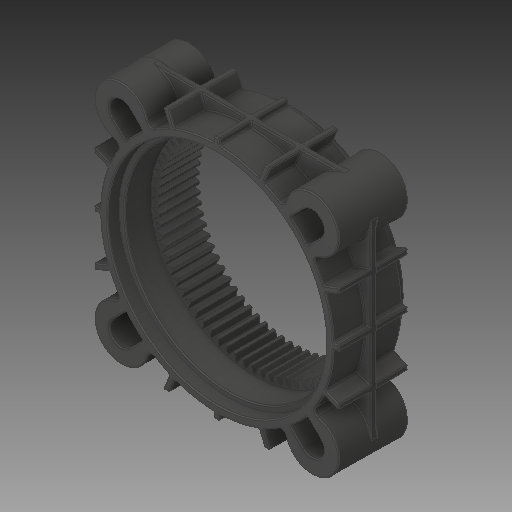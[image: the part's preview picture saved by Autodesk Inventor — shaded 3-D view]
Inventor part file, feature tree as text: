
AUTODESK INVENTOR PART (.ipt)
format: ipt  version: 2018 (Build 220112000, 112)  size: 1,989,120 bytes
history: native  units: in
note: dims shown in document units (in); Inventor stores cm internally (conversion verified against a paired STEP export)
features: fillet x1
ambient origin geometry x8: Origin, YZ Plane, XZ Plane, XY Plane, X Axis, Y Axis, Z Axis, Center Point
bodies: Solid1 (feature_tree)
feature tree (1):
  fillet  "Fillet12"  [1 undecoded]
note: 1 required parameter value undecoded (feature->parameter linkage not recoverable at this tier; creation-order binding heuristic only, values carry confidence <= 0.55)
